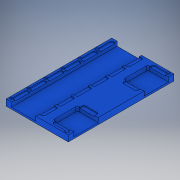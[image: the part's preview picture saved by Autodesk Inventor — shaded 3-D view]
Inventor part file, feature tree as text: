
AUTODESK INVENTOR PART (.ipt)
format: ipt  version: 2019.4 (Build 234330000, 330)  size: 296,960 bytes
history: native  units: in
note: dims shown in document units (in); Inventor stores cm internally (conversion verified against a paired STEP export)
features: extrude x5, sketch x4
ambient origin geometry x8: Origin, YZ Plane, XZ Plane, XY Plane, X Axis, Y Axis, Z Axis, Center Point
bodies: Solid1 (feature_tree)
feature tree (9):
  extrude  "Extrusion1"  Depth=8.5in
  extrude  "Extrusion7"  Depth=0.4331in
  extrude  "Extrusion8"  Depth=0.3543in TaperAngle=0.0deg
  sketch  "Sketch10"  dims[d95=0.2767in d96=1.1811in d97=0.25in d99=0.2559in d100=0.2767in d101=1.1811in d102=0.315in d105=0.125in d106=2.3622in d108=1.3712in d109=0.3937in d111=0.3937in d113=0.0787in d114=0.0in d115=1.9685in d116=0.4331in d117=1.6535in d118=0.2767in d119=1.1811in d120=0.2559in d121=0.315in d122=0.2767in d123=1.1811in d124=0.25in d125=0.125in d126=0.3543in d127=0.0in d128=0.0787in d129=0.0in]
  extrude  "Extrusion9"  Depth=1.1811in
  extrude  "Extrusion10"  Depth=0.0787in
  sketch  "Sketch1"  dims[d0=5.0in d1=8.5in]
  sketch  "Sketch8"  dims[d2=0.5in d3=0.0in d91=0.4331in]
  sketch  "Sketch9"  dims[d92=1.9685in d93=0.3543in d94=0.0in]
